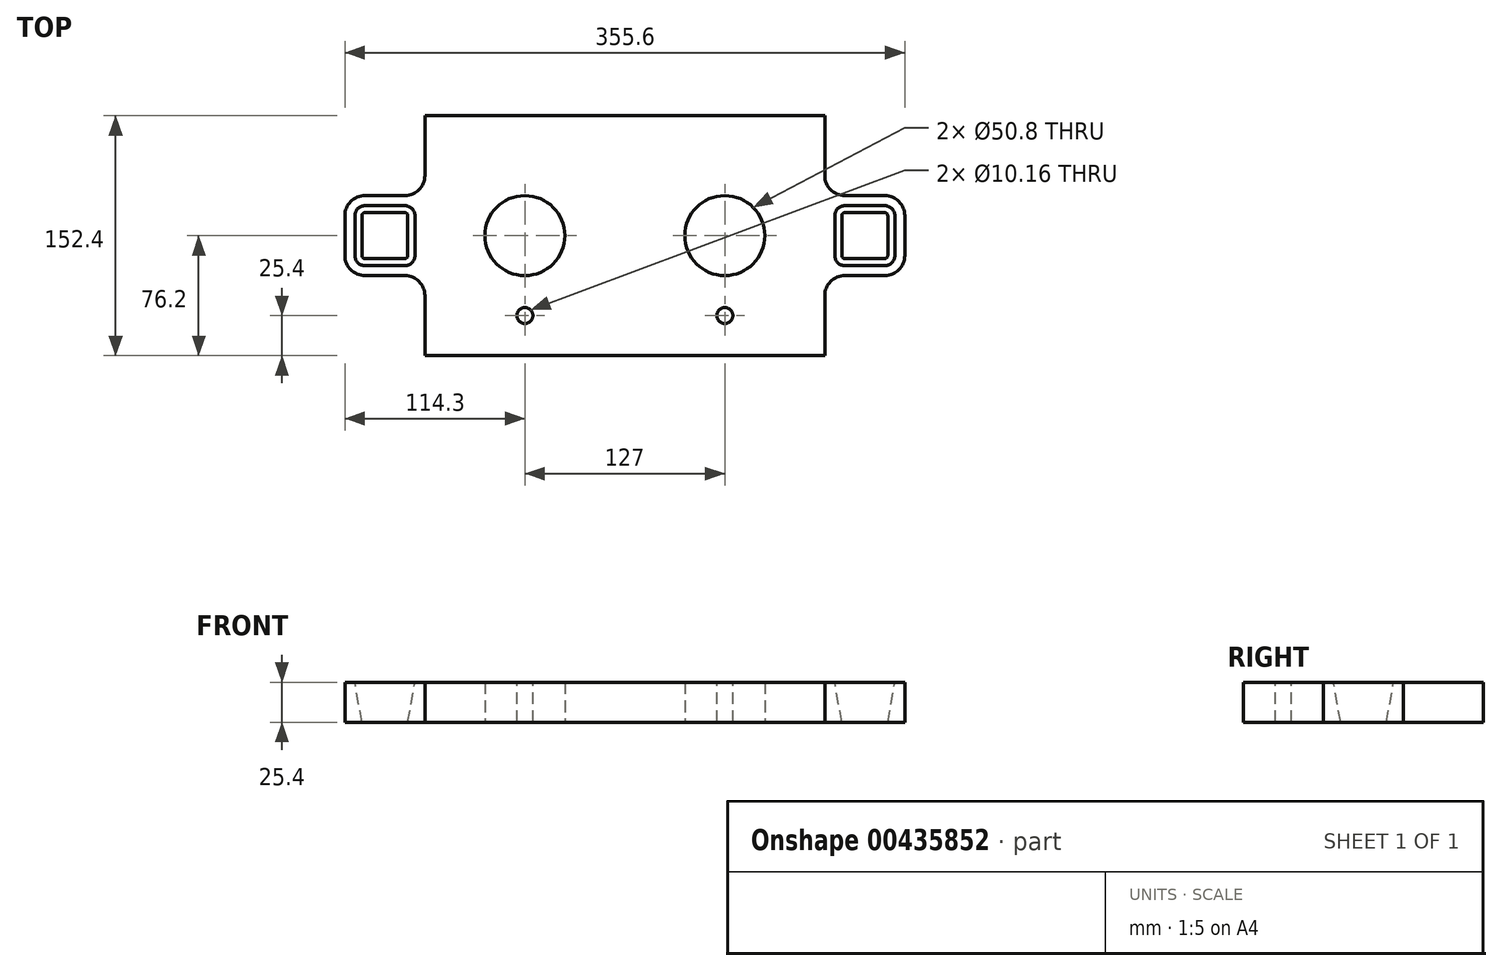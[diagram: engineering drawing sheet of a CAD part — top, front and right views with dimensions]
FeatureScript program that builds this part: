
annotation { "Feature Type Name" : "Feature", "Feature Type Description" : "" }
export const myFeature = defineFeature(function(context is Context, id is Id, definition is map)
    precondition{}
    {
        {
            var Q0;
            Q0=qCreatedBy(makeId("Top.planeOp"),FACE);
            var sketch = newSketch(context, id + "F0", { "sketchPlane" : qUnion([Q0])});
            skCircle(sketch, "E0", {"center": v(0, 0) * mm, "radius": 25.4 * mm});
            skLineSegment(sketch, "E1.bottom", {"start": v(63.5, 76.2) * mm, "end": v(-63.5, 76.2) * mm});
            skLineSegment(sketch, "E1.top", {"start": v(63.5, -76.2) * mm, "end": v(-63.5, -76.2) * mm});
            skLineSegment(sketch, "E1.left", {"start": v(63.5, 76.2) * mm, "end": v(63.5, -76.2) * mm});
            skLineSegment(sketch, "E1.right", {"start": v(-63.5, 76.2) * mm, "end": v(-63.5, -76.2) * mm});
            skLineSegment(sketch, "E2.bottom", {"start": v(63.5, -25.4) * mm, "end": v(114.3, -25.4) * mm});
            skLineSegment(sketch, "E2.top", {"start": v(63.5, 25.4) * mm, "end": v(114.3, 25.4) * mm});
            skLineSegment(sketch, "E2.left", {"start": v(63.5, -25.4) * mm, "end": v(63.5, 25.4) * mm});
            skLineSegment(sketch, "E2.right", {"start": v(114.3, -25.4) * mm, "end": v(114.3, 25.4) * mm});
            skSolve(sketch);
        }
        {
            var Q0;
            Q0=makeQuery(id+"F0.imprint","IMPRINT",FACE,{"disambiguationData":[TD([[makeQuery(id+"F0.imprint","IMPRINT",EDGE,{"derivedFrom":sQuery(id+"F0.wireOp",EDGE,"E2.bottom")}),1.0]])]});
            var Q1;
            Q1=makeQuery(id+"F0.imprint","IMPRINT",FACE,{"disambiguationData":[TD([[makeQuery(id+"F0.imprint","IMPRINT",EDGE,{"derivedFrom":sQuery(id+"F0.wireOp",EDGE,"E0")}),-1.0]])]});
            extrude(context, id + "F1", {"entities" : qUnion([Q0, Q1]), "depth" : 25.4 * mm});
        }
        {
            var Q0;
            Q0=makeQuery(id+"F1.opExtrude","SWEPT_EDGE",EDGE,{"disambiguationData":[OSD([sQuery(id+"F0.wireOp",EDGE,"E1.left"),sQuery(id+"F0.wireOp",EDGE,"E2.bottom"),sQuery(id+"F0.wireOp",EDGE,"E2.left")])]});
            var Q1;
            Q1=makeQuery(id+"F1.opExtrude","SWEPT_EDGE",EDGE,{"disambiguationData":[OSD([sQuery(id+"F0.wireOp",EDGE,"E1.left"),sQuery(id+"F0.wireOp",EDGE,"E2.top"),sQuery(id+"F0.wireOp",EDGE,"E2.left")])]});
            var Q2;
            Q2=makeQuery(id+"F1.opExtrude","SWEPT_EDGE",EDGE,{"disambiguationData":[OSD([sQuery(id+"F0.wireOp",EDGE,"E2.bottom"),sQuery(id+"F0.wireOp",EDGE,"E2.right")])]});
            var Q3;
            Q3=makeQuery(id+"F1.opExtrude","SWEPT_EDGE",EDGE,{"disambiguationData":[OSD([sQuery(id+"F0.wireOp",EDGE,"E2.top"),sQuery(id+"F0.wireOp",EDGE,"E2.right")])]});
            fillet(context, id + "F2", {"entities" : qUnion([Q0, Q1, Q2, Q3]), "radius" : 12.7 * mm, "tangentPropagation" : true, "allowEdgeOverflow" : false});
        }
        {
            var Q0;
            Q0=makeQuery(id+"F1.opExtrude","CAP_FACE",FACE,{"disambiguationData":[OSD([sQuery(id+"F0.wireOp",EDGE,"E0"),sQuery(id+"F0.wireOp",EDGE,"E1.bottom"),sQuery(id+"F0.wireOp",EDGE,"E1.top"),sQuery(id+"F0.wireOp",EDGE,"E1.left"),sQuery(id+"F0.wireOp",EDGE,"E1.right"),sQuery(id+"F0.wireOp",EDGE,"E2.bottom"),sQuery(id+"F0.wireOp",EDGE,"E2.top"),sQuery(id+"F0.wireOp",EDGE,"E2.right")])],"isStart":false});
            var sketch = newSketch(context, id + "F3", { "sketchPlane" : qUnion([Q0])});
            skPoint(sketch, "E3", {"position": v(0, -50.8) * mm});
            skLineSegment(sketch, "E4.1", {"start": v(101.6, 19.05) * mm, "end": v(76.2, 19.05) * mm});
            skArc(sketch, "E4.2", {"start": v(107.95, 12.7) * mm, "mid": v(106.1, 17.2) * mm, "end": v(101.6, 19.05) * mm});
            skLineSegment(sketch, "E4.3", {"start": v(107.95, -12.7) * mm, "end": v(107.95, 12.7) * mm});
            skArc(sketch, "E4.4", {"start": v(101.6, -19.05) * mm, "mid": v(106.1, -17.2) * mm, "end": v(107.95, -12.7) * mm});
            skLineSegment(sketch, "E4.6", {"start": v(76.2, -19.05) * mm, "end": v(101.6, -19.05) * mm});
            skLineSegment(sketch, "E5", {"start": v(69.85, -12.7) * mm, "end": v(69.85, 12.7) * mm});
            skPoint(sketch, "E6.visualSharp", {"position": v(69.85, -19.05) * mm});
            skArc(sketch, "E6.filletArc", {"start": v(69.85, -12.7) * mm, "mid": v(71.7, -17.2) * mm, "end": v(76.2, -19.05) * mm});
            skPoint(sketch, "E7.visualSharp", {"position": v(69.85, 19.05) * mm});
            skArc(sketch, "E7.filletArc", {"start": v(76.2, 19.05) * mm, "mid": v(71.7, 17.2) * mm, "end": v(69.85, 12.7) * mm});
            skSolve(sketch);
        }
        {
            var Q0;
            Q0=sQuery(id+"F3.wireOp",VERTEX,"E3");
            var Q1;
            Q1=makeQuery(id+"F1.opExtrude","SWEPT_BODY",BODY,{"disambiguationData":[OSD([sQuery(id+"F0.wireOp",EDGE,"E0"),sQuery(id+"F0.wireOp",EDGE,"E1.bottom"),sQuery(id+"F0.wireOp",EDGE,"E1.top"),sQuery(id+"F0.wireOp",EDGE,"E1.left"),sQuery(id+"F0.wireOp",EDGE,"E1.right"),sQuery(id+"F0.wireOp",EDGE,"E2.bottom"),sQuery(id+"F0.wireOp",EDGE,"E2.top"),sQuery(id+"F0.wireOp",EDGE,"E2.right")])]});
            hole(context, id + "F4", {"style" : HoleStyle.SIMPLE, "endStyle" : HoleEndStyle.THROUGH, "holeDiameter" : 10.16 * mm, "isTappedThrough" : true, "tappedDepth" : 12.7 * mm, "tapClearance" : 3, "locations" : qUnion([Q0]), "scope" : qUnion([Q1])});
        }
        {
            var Q0;
            Q0=makeQuery(id+"F3.imprint","IMPRINT",FACE,{"disambiguationData":[TD([[makeQuery(id+"F3.imprint","IMPRINT",EDGE,{"derivedFrom":sQuery(id+"F3.wireOp",EDGE,"E4.1")}),1.0]])]});
            extrude(context, id + "F5", {"entities" : qUnion([Q0]), "operationType" : NewBodyOperationType.REMOVE, "endBound" : BoundingType.THROUGH_ALL, "oppositeDirection" : true, "depth" : 25.4 * mm, "hasDraft" : true, "draftAngle" : 10 * degree, "draftPullDirection" : true});
        }
        {
            var Q0;
            Q0=makeQuery(id+"F1.opExtrude","SWEPT_BODY",BODY,{"disambiguationData":[OSD([sQuery(id+"F0.wireOp",EDGE,"E0"),sQuery(id+"F0.wireOp",EDGE,"E1.bottom"),sQuery(id+"F0.wireOp",EDGE,"E1.top"),sQuery(id+"F0.wireOp",EDGE,"E1.left"),sQuery(id+"F0.wireOp",EDGE,"E1.right"),sQuery(id+"F0.wireOp",EDGE,"E2.bottom"),sQuery(id+"F0.wireOp",EDGE,"E2.top"),sQuery(id+"F0.wireOp",EDGE,"E2.right")])]});
            var Q1;
            Q1=makeQuery(id+"F1.opExtrude","SWEPT_FACE",FACE,{"disambiguationData":[OSD([sQuery(id+"F0.wireOp",EDGE,"E1.right")])]});
            mirror(context, id + "F6", {"operationType" : NewBodyOperationType.ADD, "entities" : qUnion([Q0]), "mirrorPlane" : qUnion([Q1])});
        }
    });
